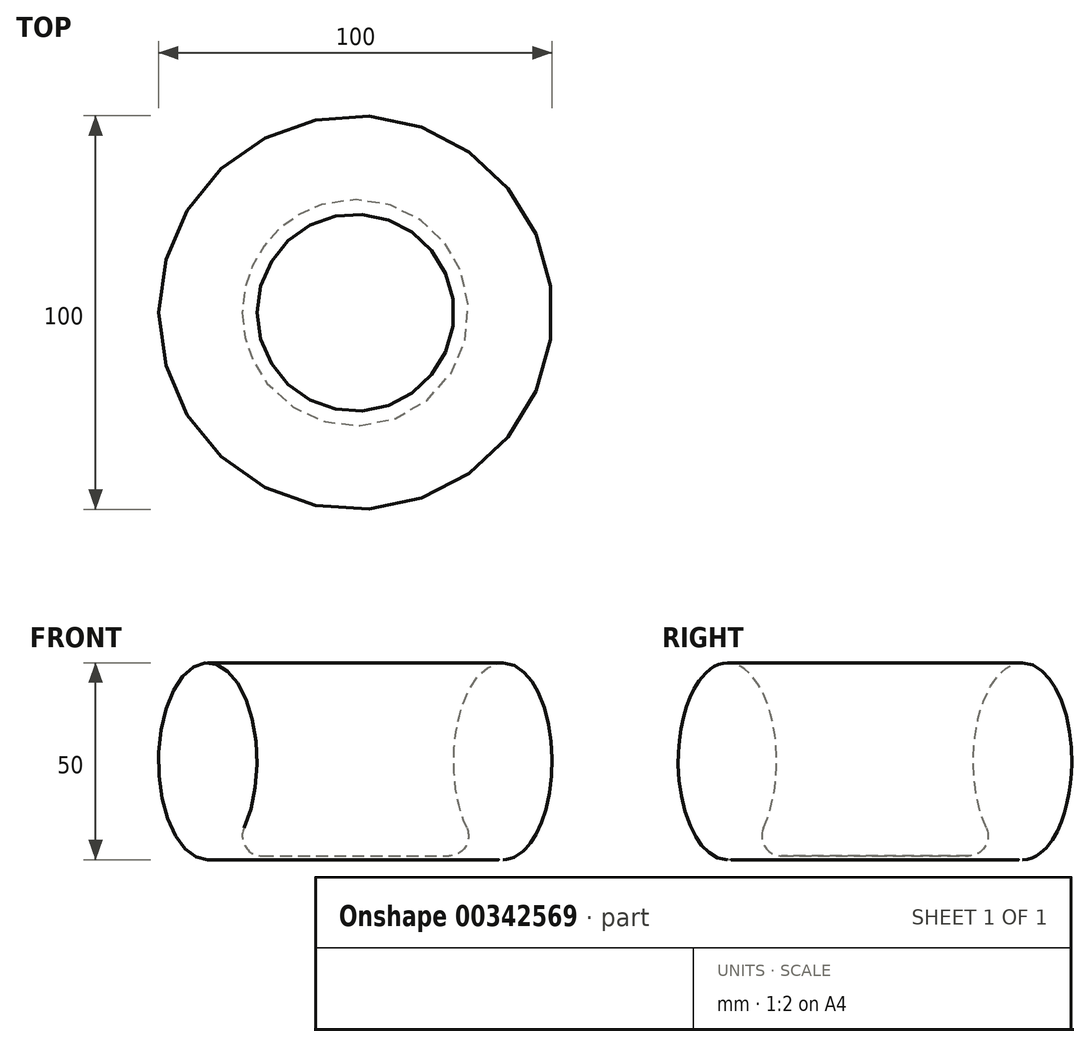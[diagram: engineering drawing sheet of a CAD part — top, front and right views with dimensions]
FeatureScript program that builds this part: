
annotation { "Feature Type Name" : "Feature", "Feature Type Description" : "" }
export const myFeature = defineFeature(function(context is Context, id is Id, definition is map)
    precondition{}
    {
        {
            var Q0;
            Q0=qCreatedBy(makeId("Front.planeOp"),FACE);
            var sketch = newSketch(context, id + "F0", { "sketchPlane" : qUnion([Q0])});
            skEllipticalArc(sketch, "E0", {});
            skLineSegment(sketch, "E1", {"start": v(0, 0) * mm, "end": v(0, 100) * mm, "construction": true});
            skPoint(sketch, "E2", {"position": v(25, 25) * mm});
            skPoint(sketch, "E3", {"position": v(50, 25) * mm});
            skLineSegment(sketch, "E4", {"start": v(37.5, 0) * mm, "end": v(0, 0) * mm});
            skLineSegment(sketch, "E5", {"start": v(0, 0) * mm, "end": v(0, 1) * mm});
            skLineSegment(sketch, "E6", {"start": v(0, 1) * mm, "end": v(23.75, 1) * mm});
            skPoint(sketch, "E7.orphan", {"position": v(37.5, 1) * mm});
            skPoint(sketch, "E8.visualSharp", {"position": v(34, 1) * mm});
            skArc(sketch, "E8.filletArc", {"start": v(23.75, 1) * mm, "mid": v(27.96, 3.3) * mm, "end": v(28.3, 8.09) * mm});
            const initialGuessF0  = {"E0": [0.0375, 0.025, 0, 1, 0.025, 0.0125, 3.141592653589793, 2.3138228204925895]};
            skSetInitialGuess(sketch, initialGuessF0);
            skSolve(sketch);
        }
        {
            var Q0;
            Q0=makeQuery(id+"F0.imprint","IMPRINT",FACE,{"disambiguationData":[TD([[makeQuery(id+"F0.imprint","IMPRINT",EDGE,{"derivedFrom":sQuery(id+"F0.wireOp",EDGE,"E0")}),1.0]])]});
            var Q1;
            Q1=makeQuery(id+"F0.imprint","IMPRINT",FACE,{"disambiguationData":[TD([[makeQuery(id+"F0.imprint","IMPRINT",EDGE,{"derivedFrom":sQuery(id+"F0.wireOp",EDGE,"793c75fe-19e5-4459-9b79-2bd3d177ff24.0")}),1.0]])]});
            var Q2;
            Q2=sQuery(id+"F0.wireOp",EDGE,"E1");
            revolve(context, id + "F1", {"entities" : qUnion([Q0, Q1]), "axis" : qUnion([Q2]), "revolveType" : RevolveType.FULL});
        }
    });
